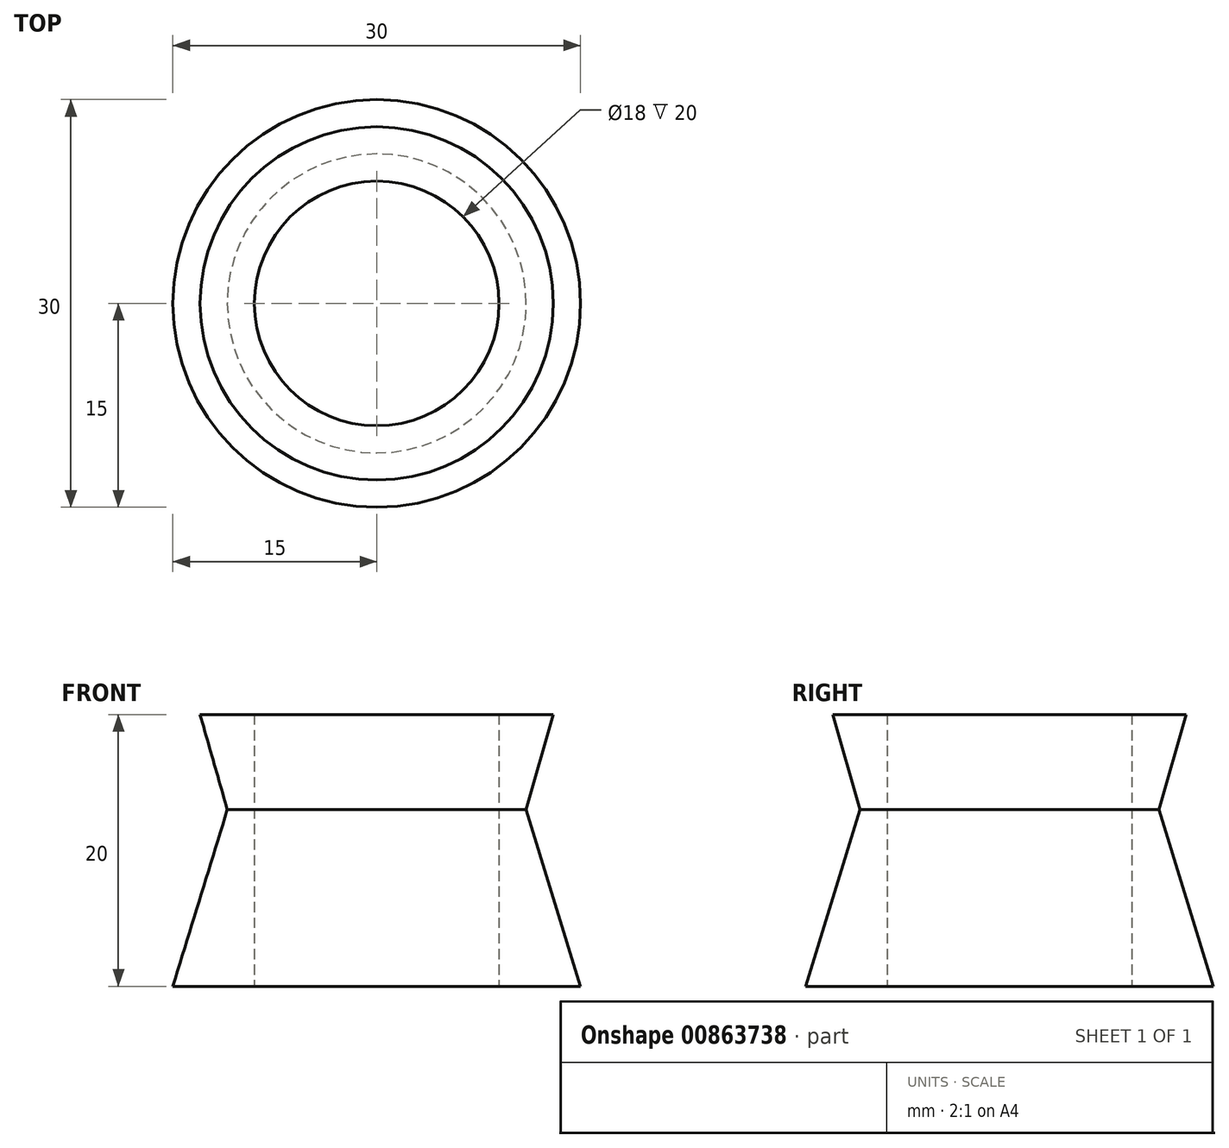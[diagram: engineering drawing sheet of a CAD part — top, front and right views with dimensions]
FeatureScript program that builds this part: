
annotation { "Feature Type Name" : "Feature", "Feature Type Description" : "" }
export const myFeature = defineFeature(function(context is Context, id is Id, definition is map)
    precondition{}
    {
        {
            var Q0;
            Q0=qCreatedBy(makeId("Front.planeOp"),FACE);
            var sketch = newSketch(context, id + "F0", { "sketchPlane" : qUnion([Q0])});
            skLineSegment(sketch, "E0", {"start": v(0, 0) * mm, "end": v(0, 30) * mm});
            skLineSegment(sketch, "E1", {"start": v(0, 0) * mm, "end": v(9, 0) * mm});
            skLineSegment(sketch, "E2", {"start": v(9, 0) * mm, "end": v(9, 20) * mm});
            skLineSegment(sketch, "E3", {"start": v(9, 20) * mm, "end": v(0, 30) * mm});
            skLineSegment(sketch, "E4", {"start": v(9, 20) * mm, "end": v(13, 20) * mm});
            skLineSegment(sketch, "E5", {"start": v(9, 0) * mm, "end": v(15, 0) * mm});
            skLineSegment(sketch, "E6", {"start": v(9, 0) * mm, "end": v(9, 13) * mm, "construction": true});
            skLineSegment(sketch, "E7", {"start": v(9, 13) * mm, "end": v(11, 13) * mm, "construction": true});
            skLineSegment(sketch, "E8", {"start": v(11, 13) * mm, "end": v(13, 20) * mm});
            skLineSegment(sketch, "E9", {"start": v(15, 0) * mm, "end": v(11, 13) * mm});
            skSolve(sketch);
        }
        {
            var Q0;
            Q0=makeQuery(id+"F0.imprint","IMPRINT",FACE,{"disambiguationData":[TD([[makeQuery(id+"F0.imprint","IMPRINT",EDGE,{"derivedFrom":sQuery(id+"F0.wireOp",EDGE,"E2")}),-1.0]])]});
            var Q1;
            Q1=sQuery(id+"F0.wireOp",EDGE,"E0");
            revolve(context, id + "F1", {"surfaceOperationType" : NewSurfaceOperationType.NEW, "entities" : qUnion([Q0]), "axis" : qUnion([Q1]), "revolveType" : RevolveType.FULL});
        }
    });
